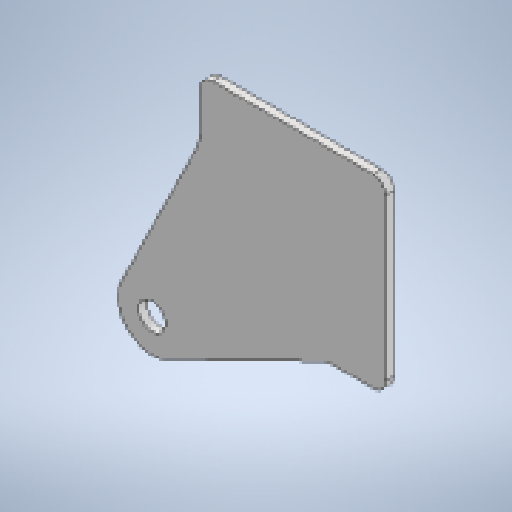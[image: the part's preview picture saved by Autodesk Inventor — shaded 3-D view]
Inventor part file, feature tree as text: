
AUTODESK INVENTOR PART (.ipt)
format: ipt  version: 2025 (Build 290162010, 162A)  size: 295,424 bytes
history: native  units: mm
features: other x2, sheet_metal_op x1, chamfer x1, sketch x1
ambient origin geometry x8: Origin, YZ Plane, XZ Plane, XY Plane, X Axis, Y Axis, Z Axis, Center Point
bodies: Solid1 (feature_tree)
feature tree (5):
  sheet_metal_op  "Face1"
  chamfer  "Corner Round3"
  sketch  "Sketch1"  dims[d2=80.0mm d3=80.0mm d6=4.0mm d29=5.0mm d30=13.0mm d31=10.0mm d32=40.0mm d34=5.0mm d35=15.0mm d36=25.0mm d37=6.0mm]
  other  "Plate1"
  other  "Definition1"
